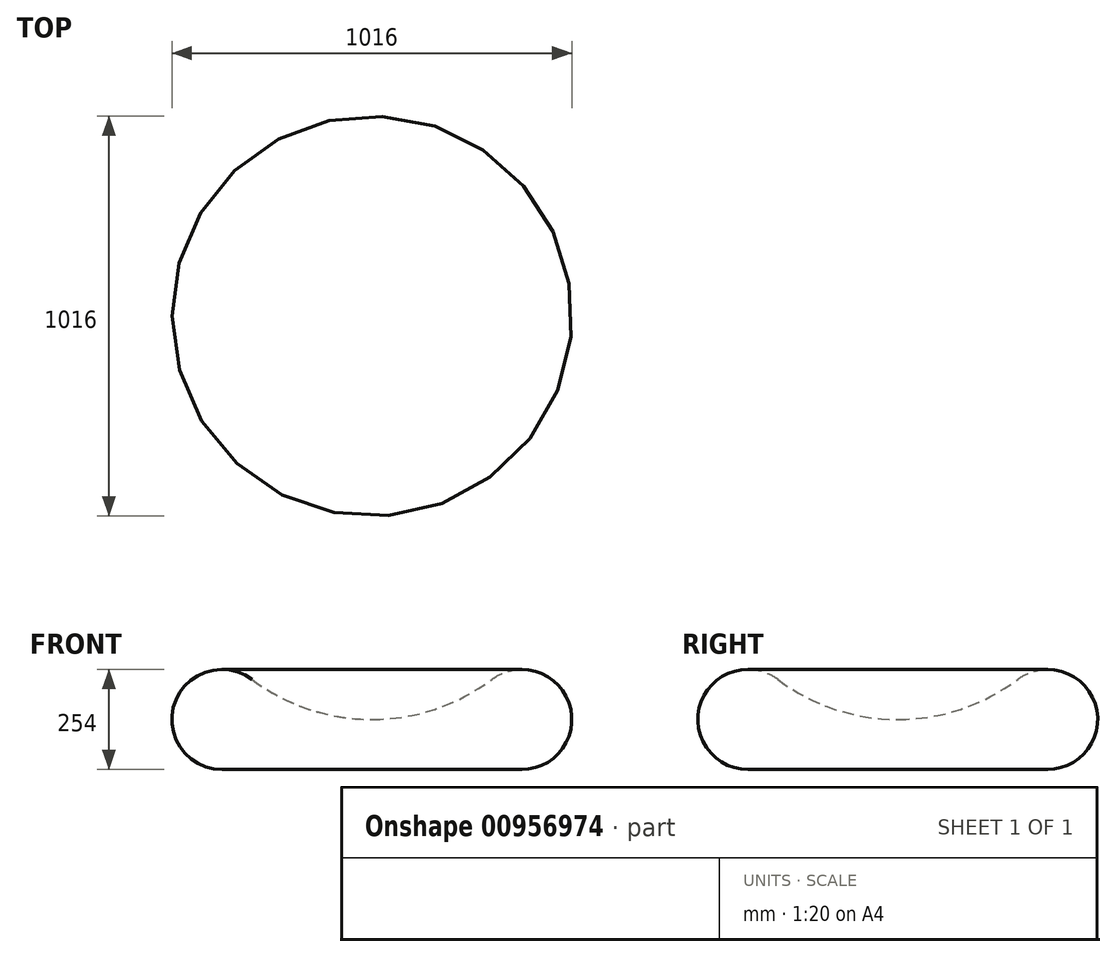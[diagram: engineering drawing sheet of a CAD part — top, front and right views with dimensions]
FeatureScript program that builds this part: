
annotation { "Feature Type Name" : "Feature", "Feature Type Description" : "" }
export const myFeature = defineFeature(function(context is Context, id is Id, definition is map)
    precondition{}
    {
        {
            var Q0;
            Q0=qCreatedBy(makeId("Front.planeOp"),FACE);
            var sketch = newSketch(context, id + "F0", { "sketchPlane" : qUnion([Q0])});
            skArc(sketch, "E0", {"start": v(-304.8, 228.6) * mm, "mid": v(-160.64, 153.07) * mm, "end": v(0, 127) * mm});
            skArc(sketch, "E1", {"start": v(-304.8, 228.6) * mm, "mid": v(-501.48, 167.16) * mm, "end": v(-381, 0) * mm});
            skLineSegment(sketch, "E2", {"start": v(0, 0) * mm, "end": v(0, 127) * mm});
            skLineSegment(sketch, "E3", {"start": v(0, 0) * mm, "end": v(-381, 0) * mm});
            skSolve(sketch);
        }
        {
            var Q0;
            Q0=makeQuery(id+"F0.imprint","IMPRINT",FACE,{"disambiguationData":[TD([[makeQuery(id+"F0.imprint","IMPRINT",EDGE,{"derivedFrom":sQuery(id+"F0.wireOp",EDGE,"E0")}),-1.0]])]});
            var Q1;
            Q1=sQuery(id+"F0.wireOp",EDGE,"E2");
            revolve(context, id + "F1", {"surfaceOperationType" : NewSurfaceOperationType.NEW, "entities" : qUnion([Q0]), "axis" : qUnion([Q1]), "revolveType" : RevolveType.FULL});
        }
        {
            var Q0;
            Q0=qCreatedBy(makeId("Front.planeOp"),FACE);
            var sketch = newSketch(context, id + "F2", { "sketchPlane" : qUnion([Q0])});
            skCircle(sketch, "E4", {"center": v(-381, 127) * mm, "radius": 126 * mm});
            skSolve(sketch);
        }
        {
            var Q0;
            Q0=sQuery(id+"F2.wireOp",EDGE,"E4");
            var Q1;
            Q1=sQuery(id+"F0.wireOp",EDGE,"E2");
            revolve(context, id + "F3", {"bodyType" : ToolBodyType.SURFACE, "surfaceOperationType" : NewSurfaceOperationType.NEW, "surfaceEntities" : qUnion([Q0]), "axis" : qUnion([Q1]), "revolveType" : RevolveType.FULL});
        }
    });
